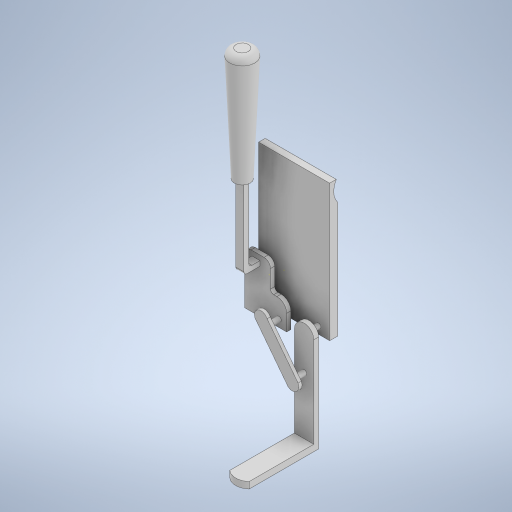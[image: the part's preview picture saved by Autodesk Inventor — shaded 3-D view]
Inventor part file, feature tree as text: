
AUTODESK INVENTOR PART (.ipt)
format: ipt  version: 2023 (Build 270158000, 158)  size: 434,688 bytes
history: native  units: in
note: dims shown in document units (in); Inventor stores cm internally (conversion verified against a paired STEP export)
features: sketch x18, extrude x16, fillet x3, draft x1, direct_edit x1, other x1
ambient origin geometry x8: Origin, YZ Plane, XZ Plane, XY Plane, X Axis, Y Axis, Z Axis, Center Point
bodies: Solid1 (feature_tree)
feature tree (40):
  extrude  "Extrusion1"  Depth=1.6624in
  extrude  "Extrusion2"  Depth=0.875in
  extrude  "Extrusion3"  Depth=0.0591in
  extrude  "Extrusion4"  Depth=0.315in
  sketch  "Sketch5"  dims[d11=0.315in d12=0.6496in]
  extrude  "Extrusion5"  Depth=0.6496in
  extrude  "Extrusion6"  Depth=0.0787in
  extrude  "Extrusion7"  Depth=0.0394in
  extrude  "Extrusion8"  Depth=0.1181in TaperAngle=0.0deg
  sketch  "Sketch10"  dims[d25=1.1811in d26=0.0591in d27=0.0in d28=0.0591in]
  extrude  "Extrusion9"  Depth=0.1181in TaperAngle=0.0deg
  fillet  "Fillet1"  Radius=0.1181in
  fillet  "Fillet2"  Radius=0.1181in
  extrude  "Extrusion10"  Depth=0.0591in TaperAngle=0.0deg
  draft  "FaceDraft1"
  fillet  "Fillet3"  Radius=0.0591in
  extrude  "Extrusion11"  Depth=0.1181in
  extrude  "Extrusion12"  Depth=0.0591in
  extrude  "Extrusion13"  Depth=0.1969in TaperAngle=0.0deg
  extrude  "Extrusion14"  Depth=0.0591in TaperAngle=0.0deg
  extrude  "Extrusion15"  Depth=0.0394in
  extrude  "Extrusion16"  Depth=0.315in
  direct_edit  "Direct Edit1"
  sketch  "Sketch1"  dims[d0=0.8661in d1=1.6624in]
  sketch  "Sketch2"  dims[d2=0.0984in d3=0.0in d4=0.875in]
  sketch  "Sketch3"  dims[d5=0.0in d6=0.0in d7=0.0591in]
  sketch  "Sketch4"  dims[d8=0.1181in d9=0.0in d10=0.315in]
  sketch  "Sketch6"  dims[d13=0.5118in d14=0.0787in]
  sketch  "Sketch7"  dims[d15=0.0787in d16=0.0394in]
  sketch  "Sketch8"  dims[d17=0.1181in d18=0.0512in d19=0.0in]
  sketch  "Sketch9"  dims[d20=0.0591in d21=0.1181in d22=0.0in d23=0.1181in d24=0.1181in]
  sketch  "Sketch11"  dims[d29=0.1181in d30=0.0in d31=0.0984in]
  sketch  "Sketch12"  dims[d32=0.0591in d33=0.0591in]
  sketch  "Sketch13"  dims[d34=0.0886in d35=0.1969in d36=0.0in]
  sketch  "Sketch14"  dims[d37=0.0591in d38=0.9252in d39=0.0in]
  sketch  "Sketch15"  dims[d40=0.0394in d41=0.0394in]
  sketch  "Sketch16"  dims[d42=0.0295in d43=0.315in]
  sketch  "Sketch17"  dims[d44=1.378in d45=0.0in]
  sketch  "Sketch18"  dims[d46=0.0172in d47=0.0787in d48=0.5118in d49=0.0591in d50=0.1181in d51=0.0in d52=0.1575in d54=0.0394in d55=0.0in d56=0.0787in d57=0.7874in d58=0.0in d59=0.1737in d60=0.0787in d61=0.0in d62=0.3937in d63=0.0in d64=0.4375in d65=0.0in d66=0.0in d67=0.7874in d68=0.3937in d69=0.3937in]
  other  "Scale1"
